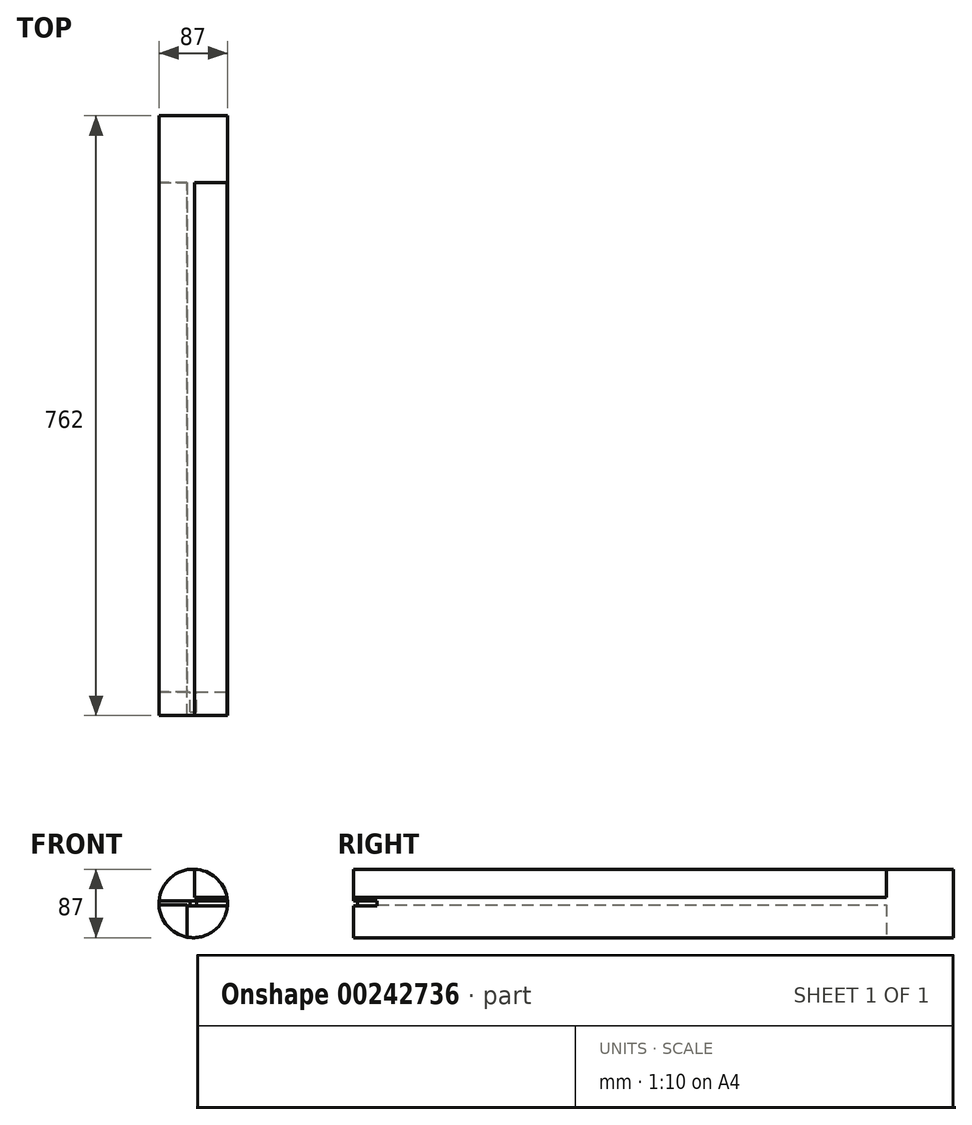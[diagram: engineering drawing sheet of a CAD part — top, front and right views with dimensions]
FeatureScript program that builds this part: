
annotation { "Feature Type Name" : "Feature", "Feature Type Description" : "" }
export const myFeature = defineFeature(function(context is Context, id is Id, definition is map)
    precondition{}
    {
        {
            var Q0;
            Q0=qCreatedBy(makeId("Front.planeOp"),FACE);
            var sketch = newSketch(context, id + "F0", { "sketchPlane" : qUnion([Q0])});
            skCircle(sketch, "E0", {"center": v(0, 0) * mm, "radius": 43.5 * mm});
            skSolve(sketch);
        }
        {
            var Q0;
            Q0 = qSketchRegion(id + "F0", true);
            extrude(context, id + "F1", {"entities" : qUnion([Q0]), "depth" : (30 * 25.4) * mm});
        }
        {
            var Q0;
            Q0=makeQuery(id+"F1.opExtrude","CAP_FACE",FACE,{"disambiguationData":[OSD([sQuery(id+"F0.wireOp",EDGE,"E0")])],"isStart":false});
            var sketch = newSketch(context, id + "F2", { "sketchPlane" : qUnion([Q0])});
            skLineSegment(sketch, "E1.bottom", {"start": v(-49.5, -3) * mm, "end": v(49.5, -3) * mm});
            skLineSegment(sketch, "E1.top", {"start": v(-49.5, 3) * mm, "end": v(49.5, 3) * mm});
            skLineSegment(sketch, "E1.left", {"start": v(-49.5, -3) * mm, "end": v(-49.5, 3) * mm});
            skLineSegment(sketch, "E1.right", {"start": v(49.5, -3) * mm, "end": v(49.5, 3) * mm});
            skPoint(sketch, "E1.middle", {"position": v(0, 0) * mm});
            skSolve(sketch);
        }
        {
            var Q0;
            Q0 = qSketchRegion(id + "F2", true);
            extrude(context, id + "F3", {"entities" : qUnion([Q0]), "operationType" : NewBodyOperationType.REMOVE, "oppositeDirection" : true, "depth" : 30 * mm});
        }
        {
            var Q0;
            Q0=makeQuery(id+"F3.boolean.opBoolean","COPY",FACE,{"derivedFrom":makeQuery(id+"F3.opExtrude","CAP_FACE",FACE,{"disambiguationData":[OSD([sQuery(id+"F2.wireOp",EDGE,"E1.bottom"),sQuery(id+"F2.wireOp",EDGE,"E1.top"),sQuery(id+"F2.wireOp",EDGE,"E1.left"),sQuery(id+"F2.wireOp",EDGE,"E1.right")])],"isStart":false})});
            var sketch = newSketch(context, id + "F4", { "sketchPlane" : qUnion([Q0])});
            skLineSegment(sketch, "E2.bottom", {"start": v(-3.97, -3) * mm, "end": v(3.97, -3) * mm});
            skLineSegment(sketch, "E2.top", {"start": v(-3.97, 3) * mm, "end": v(3.97, 3) * mm});
            skLineSegment(sketch, "E2.left", {"start": v(-3.97, -3) * mm, "end": v(-3.97, 3) * mm});
            skLineSegment(sketch, "E2.right", {"start": v(3.97, -3) * mm, "end": v(3.97, 3) * mm});
            skPoint(sketch, "E2.middle", {"position": v(0, 0) * mm});
            skSolve(sketch);
        }
        {
            var Q0;
            Q0 = qSketchRegion(id + "F4", true);
            extrude(context, id + "F5", {"entities" : qUnion([Q0]), "operationType" : NewBodyOperationType.ADD, "depth" : 25 * mm});
        }
        {
            var Q0;
            {var subQ0=sQuery(id+"F0.wireOp",EDGE,"E0");Q0=makeQuery(id+"F3.boolean.opBoolean","SPLIT",FACE,{"disambiguationData":[TD([makeQuery(id+"F3.opExtrude","SWEPT_FACE",FACE,{"disambiguationData":[OSD([sQuery(id+"F2.wireOp",EDGE,"E1.top")])]})])],"derivedFrom":makeQuery(id+"F1.opExtrude","CAP_FACE",FACE,{"disambiguationData":[OSD([subQ0])],"isStart":false})});}
            var sketch = newSketch(context, id + "F6", { "sketchPlane" : qUnion([Q0])});
            skLineSegment(sketch, "E3.bottom", {"start": v(1.62, 7.67) * mm, "end": v(45.22, 7.67) * mm});
            skLineSegment(sketch, "E3.top", {"start": v(1.62, 59.78) * mm, "end": v(45.22, 59.78) * mm});
            skLineSegment(sketch, "E3.left", {"start": v(1.62, 7.67) * mm, "end": v(1.62, 59.78) * mm});
            skLineSegment(sketch, "E3.right", {"start": v(45.22, 7.67) * mm, "end": v(45.22, 59.78) * mm});
            skPoint(sketch, "E4.middle", {"position": v(23.42, 59.78) * mm});
            skPoint(sketch, "E4.cornerSnap0", {"position": v(23.42, 59.78) * mm});
            skLineSegment(sketch, "E5", {"start": v(0, 0) * mm, "end": v(-44.24, 44.24) * mm});
            skLineSegment(sketch, "E6", {"start": v(0, 0) * mm, "end": v(-109.5, 0) * mm});
            skLineSegment(sketch, "E7.MirrorCS", {"start": v(-7.67, -1.62) * mm, "end": v(-7.67, -45.22) * mm});
            skLineSegment(sketch, "E8.MirrorCS", {"start": v(-7.67, -1.62) * mm, "end": v(-59.78, -1.62) * mm});
            skLineSegment(sketch, "E9.MirrorCS", {"start": v(-59.78, -1.62) * mm, "end": v(-59.78, -45.22) * mm});
            skLineSegment(sketch, "E10.MirrorCS", {"start": v(-7.67, -45.22) * mm, "end": v(-59.78, -45.22) * mm});
            skSolve(sketch);
        }
        {
            var Q0;
            Q0 = qSketchRegion(id + "F6", true);
            extrude(context, id + "F7", {"entities" : qUnion([Q0]), "operationType" : NewBodyOperationType.REMOVE, "oppositeDirection" : true, "depth" : 677 * mm});
        }
    });
